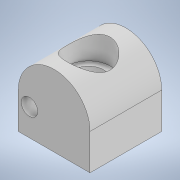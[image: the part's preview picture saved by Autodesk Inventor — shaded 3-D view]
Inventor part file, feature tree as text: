
AUTODESK INVENTOR PART (.ipt)
format: ipt  version: 2022 (Build 260153000, 153)  size: 137,728 bytes
history: native  units: mm
features: extrude x3, sketch x3, fillet x1
ambient origin geometry x8: Origin, YZ Plane, XZ Plane, XY Plane, X Axis, Y Axis, Z Axis, Center Point
bodies: Solid1 (feature_tree)
feature tree (7):
  extrude  "Extrusion1"  Depth=4.8mm
  extrude  "Extrusion2"  Depth=5.0mm
  fillet  "Fillet1"  Radius=10.0mm
  extrude  "Extrusion3"  Depth=5.0mm
  sketch  "Sketch1"  dims[d0=4.2mm d1=4.8mm]
  sketch  "Sketch2"  dims[d2=9.6mm d3=5.0mm d4=10.0mm]
  sketch  "Sketch3"  dims[d5=10.0mm d6=0.0mm d7=6.0mm d8=3.5mm d9=0.0mm d10=5.0mm d12=0.0mm d13=0.0mm d14=2.3mm]
